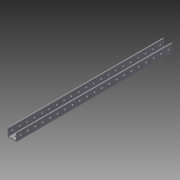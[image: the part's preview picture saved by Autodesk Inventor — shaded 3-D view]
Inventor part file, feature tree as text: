
AUTODESK INVENTOR PART (.ipt)
format: ipt  version: 2014 (Build 180170000, 170)  size: 156,672 bytes
history: native  units: in
note: dims shown in document units (in); Inventor stores cm internally (conversion verified against a paired STEP export)
features: sketch x3, hole x2, extrude x1, pattern_linear x1
ambient origin geometry x8: Origin, YZ Plane, XZ Plane, XY Plane, X Axis, Y Axis, Z Axis, Center Point
bodies: Solid1 (feature_tree)
feature tree (7):
  extrude  "Extrusion1"  Depth=21.0in TaperAngle=0.0deg
  hole  "Hole1"  [1 undecoded]
  hole  "Hole2"  [1 undecoded]
  pattern_linear  "Rectangular Pattern1"  [2 undecoded]
  sketch  "Sketch1"  dims[d0=1.25in d1=1.125in d2=0.0625in d3=0.125in d4=21.0in d5=0.0in]
  sketch  "Sketch2"  dims[d6=0.5in]
  sketch  "Sketch3"  dims[d7=0.25in d8=0.75in d9=0.375in d10=0.25in d11=0.5635in d12=1.0in d13=0.8108in d14=0.5in d15=0.25in d16=0.75in d17=0.375in d18=0.25in d19=0.5635in d20=1.0in d21=0.8108in d22=8.2677in d24=1.0in]
note: 4 required parameter values undecoded (feature->parameter linkage not recoverable at this tier; creation-order binding heuristic only, values carry confidence <= 0.55)
